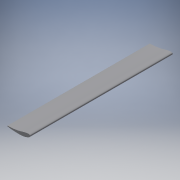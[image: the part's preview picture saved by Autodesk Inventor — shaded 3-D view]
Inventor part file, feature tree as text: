
AUTODESK INVENTOR PART (.ipt)
format: ipt  version: 2018.2 (Build 222227000, 227)  size: 150,528 bytes
history: native  units: mm
features: other x4, extrude x1, mirror x1, sketch x1, projected_geometry x1
ambient origin geometry x8: Origin, YZ Plane, XZ Plane, XY Plane, X Axis, Y Axis, Z Axis, Center Point
bodies: Body1 (feature_tree)
feature tree (8):
  other  "main frap.ipt"
  extrude  "押し出し2"  Depth=4.0mm
  mirror  "ミラー2"
  other  "ソリッド1::main frap.ipt"
  other  "TaggingFeature1"
  sketch  "スケッチ2"
  projected_geometry  "投影ループ2"
  other  "ソリッド1"
